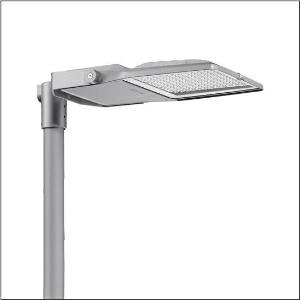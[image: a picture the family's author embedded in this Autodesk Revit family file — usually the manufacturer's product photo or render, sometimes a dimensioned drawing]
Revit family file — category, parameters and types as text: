
# Revit family: floodlight_fl_21_iq_midi___pl61_5xa7782e4c3a_83e0
name_source: partatom
category: Lighting Fixtures
units: mm (PartAtom-declared; Revit-internal decimal feet)

## family parameters
Cut with Voids When Loaded = No
Host = Face
Light Source = No
Part Type = Normal
Room Calculation Point = No
Round Connector Dimension = Use Diameter
Shared = No

## types (1)
- --- (1 x LED, 27490 lm, 208.1 W, 4000K)
    Apparent Load = 208 VA
    CIE Flux Codes = 33 65 98 100 100
    Color Rendering = 70
    Color Temperature = 4000K
    Default Elevation = 1800 mm
    Description = Floodlight FL 21 iQ midi, floodlight, primary light control with lens, of PMMA, primary optical cover: protective disc, of toughened safety glass, transparent, light distribution: PL61, light emission: direct distribution, installation type: surface-mounted, lamps: LED, High Power LED, rated values: 27.490lm | 208,1W | 132,1lm/W (begin service life); end service life: 27.490lm | 227,1W; at 50% lumin. flux: 13.745lm | 90,3W | 152,2lm/W, colour temperature: 4000K, colour rendering: CRI > 70, light colour: 740, light setting 1 begin service life: 100% | 27.490lm | 208,1W | 132,1lm/W | 4.000K, light setting 1 end service life: 227,1W, further light settings possible, control: optimised constant luminous flux control (CLO 2.0), Desk-Remote (wireless, voltage-free reading and setting of iQ features in the workshop via application-optimized NFC function/RFID function), Smart-Wire, Night-Set, Temp-Guard, Auto-Match, Street-Remote, pre-setting: linear dimming characteristic, with terminal, 6-pole, mains connection: 220..240V, AC, 50/60Hz, luminaire housing, of diecast aluminium, powder-coated, SITECO metallic grey (DB 702S), corrosivity category C5 mid according to DIN EN ISO 12944suitable for swimming poolschlorine-resistant, sealing non-destructively replaceable, please order mast flange separately, mast bracket, of steel, galvanised, powder-coated, SITECO metallic grey (DB 702S), protection rating (complete): IP66, insulation class (complete): insulation class II (safety insulation), certification: CE, ENEC, VDE, protection symbol: D, impact resistance: IK08, permissible operating ambient temperature: -40..+40°C, permissible operating ambient temperature for outdoor applications: -40..+50°C, standard: DIN EN 12944, LABS conformity tested according to VDMA 24364:2018-05, packaging unit: 1 piece

Light Distribution: PL61
    Height = 76 mm
    Lamp = 1 x LED
    Lamp Light Flux = 27490 lm
    Lamp Power = 208.1 W
    Lamp count = 1
    Length = 657 mm
    Luminous efficacy = 132 lm/W
    Manufacturer = Siteco
    ModVariant = No
    Model = 5XA7782E4C3A
    Mounting Place = Pole
    Mounting Type = Pole annexe
    Number of Poles = 1
    OnlyDefault = Yes
    Power Factor = 1
    Product Name = Floodlight FL 21 iQ midi | PL61
    Product group = floodlight | pylon annexe
    ProductGroupID = 6201
    Protection Class = Protection class II
    Protection Degree = IP 66
    RLX_Detail_Level = 1
    RLX_Emergency_Light_Flux = 0 lm
    RLX_Emergency_Type = 0
    RLX_Emergency_Type_DB = No
    RlxData = <blob elided: 153973 chars, md5=9c5039d9>
    Socket = socket
    Standby Power = 0 W
    System Light Flux = 27490 lm
    System Power = 208 W
    Type Comments = factory setting: luminous flux: 100 % | dim-lin: 254 | 710 mA
    Type Image = l_1007123.jpg
    URL = http://relux.com
    VarID = @adj_110135
    Voltage = 0 V
    Weight = 0.00 kg
    Width = 442 mm

## geometry (parser evidence)
native form markers: Blend x4, Sweep x13
no freeform markers — native parametric forms only
